# Revit family: AMX 4 HH BDE
name_source: partatom
category: Mechanical Equipment
units: mm (PartAtom-declared; Revit-internal decimal feet)

## family parameters
Always vertical = Yes
Cut with Voids When Loaded = No
OmniClass Number = 23.75.00.00
OmniClass Title = Climate Control (HVAC)
Part Type = Normal
Room Calculation Point = No
Round Connector Dimension = Use Diameter
Shared = No
Work Plane-Based = No

## types (1)
- AMX 4 HH BDE
    Condensate = 6 mm  [stored 0.019685 ft]
    Electrical connection = 1 ~ 230 V / N / PE / 50 Hz
    Exhaust Air = 200 mm
    L-C Duct Exhaust = 462 mm  [stored 1.51575 ft]
    Manufacturer = Airmaster A/S
    Max. flow rate 30 dB(A) with ePM10 50% filters = 220 m³
    Max. flow rate 30 dB(A) with ePM10 55% filters = 288 m³
    Max. flow rate 35 dB(A) with ePM10 50% filters = 220 m³
    Max. flow rate 35 dB(A) with ePM10 55% filters = 284 m³
    Model = AMX 4 HHBDE
    Network Conection = AWG 24 CAT 5e STP
    Nominal current, air handling unit = 1,79A / 2,51A / 3,5A
    Phase 1 - Max Current = 11,2 A
    Phase 1 - Max Power Consumption = 2560 W
    R-C Duct Supply = 132 mm  [stored 0.433071 ft]
    Suply Air In = 200 mm
    T-C Duct Exhaust = 114 mm  [stored 0.374016 ft]
    T-C Duct Supply = 114 mm  [stored 0.374016 ft]
    Total Depth = 1100 mm
    Total Hight = 358 mm  [stored 1.17454 ft]
    Total Width = 2055 mm  [stored 6.74213 ft]
    URL = www.airmaster-as.com
    Water Heater Surface IN = 15 mm  [stored 0.0492126 ft]
    Water Heater Surface Return = 15 mm  [stored 0.0492126 ft]
    Weight (Standard Unit) = 85

note: [stored X ft] marks values corroborated as IEEE doubles in the binary element streams (Revit-internal decimal feet)

## geometry (parser evidence)
native form markers: Sweep x6
no freeform markers — native parametric forms only
